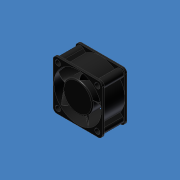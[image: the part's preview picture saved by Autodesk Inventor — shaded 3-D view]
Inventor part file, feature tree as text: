
AUTODESK INVENTOR PART (.ipt)
format: ipt  version: 2011 SP1 (Build 150282100, 282)  size: 367,104 bytes
history: native  units: mm (DEFAULTED — no unit token found)
features: sketch x10, extrude x6, hole x2, pattern_circular x2, fillet x2, revolve x1, plane x1, helix x1
ambient origin geometry x8: Origin, YZ Plane, XZ Plane, XY Plane, X Axis, Y Axis, Z Axis, Center Point
bodies: Solid1 (feature_tree)
feature tree (25):
  extrude  "Extrusion1"  Depth=20.066mm TaperAngle=0.0deg
  revolve  "Revolution1"  [1 undecoded]
  hole  "Hole3"  [1 undecoded]
  extrude  "Extrusion3"  Depth=32.004mm
  pattern_circular  "Circular Pattern2"  Count=4 Angle=360.0deg
  fillet  "Fillet2"  Radius=3.175mm
  hole  "Hole4"  [1 undecoded]
  extrude  "Extrusion4"  Depth=12.446mm
  extrude  "Extrusion5"  Depth=12.065mm
  extrude  "Extrusion6"  Depth=1.4732mm
  extrude  "Extrusion7"  TaperAngle=135.0deg  [1 undecoded]
  fillet  "Fillet3"  Radius=12.065mm
  plane  "Work Plane1"
  helix  "Coil2"  [1 undecoded]
  pattern_circular  "Circular Pattern4"  [2 undecoded]
  sketch  "Sketch1"  dims[d0=39.878mm d1=20.066mm d2=0.0mm]
  sketch  "Sketch2"  dims[d3=1.7018mm d4=12.7mm]
  sketch  "Sketch6"  dims[d5=1.7018mm d6=90.0deg]
  sketch  "Sketch7"  dims[d28=32.004mm d29=32.004mm]
  sketch  "Sketch8"  dims[d30=4.318mm d31=12.7mm d32=9.525mm d33=6.35mm d34=14.3117mm d35=19.05mm d36=20.594885mm]
  sketch  "Sketch9"  dims[d37=6.35mm]
  sketch  "Sketch10"  dims[d38=19.812mm d39=0.0mm d40=40.0mm d42=360.0deg d43=3.175mm]
  sketch  "Sketch11"  dims[d44=38.481mm d45=12.7mm d46=9.525mm d47=6.35mm d48=14.3117mm d49=19.05mm d50=20.594885mm d51=24.13mm]
  sketch  "Sketch12"  dims[d52=1.4732mm d53=1.4732mm d54=12.446mm]
  sketch  "Sketch13"  dims[d55=5.9944mm d57=12.065mm d58=12.065mm d59=1.4732mm d60=135.0deg d61=12.065mm d62=12.065mm d63=3.81mm d64=0.0mm d65=1.016mm d66=1.016mm d67=1.016mm d68=1.016mm d69=2.032mm d70=0.0mm d71=1.0922mm d72=2.54mm d73=0.0mm d74=23.876mm d75=16.256mm d76=0.0mm d77=0.7874mm d83=0.698132mm d84=2.094395mm d85=37.338mm d86=0.254mm d98=-0.762mm d99=25.4mm d100=13.97mm d101=1.5mm d102=0.0mm d103=90.0deg d104=90.0deg d105=0.0mm d106=0.0mm d107=50.0mm d109=360.0deg]
note: 7 required parameter values undecoded (feature->parameter linkage not recoverable at this tier; creation-order binding heuristic only, values carry confidence <= 0.55)